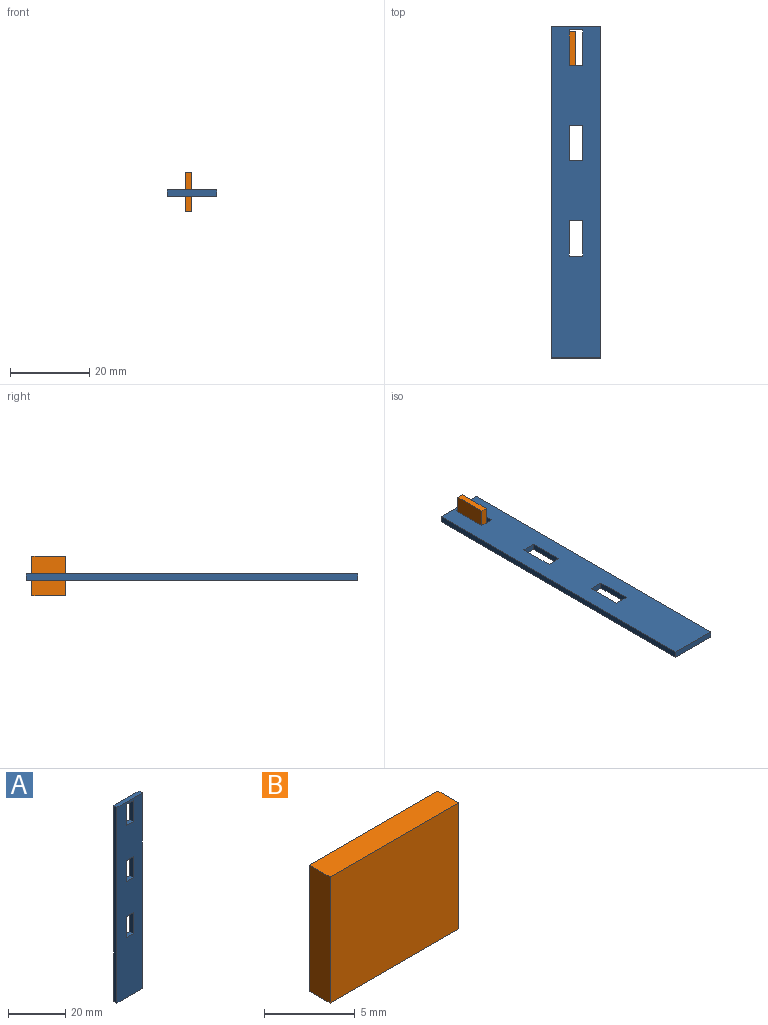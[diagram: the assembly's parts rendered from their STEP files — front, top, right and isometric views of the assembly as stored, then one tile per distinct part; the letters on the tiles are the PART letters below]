
ASSEMBLY  parts=2 mates=2
PART A: 18 faces, bbox 12.5x1.6x83.7 mm
  f0: plane 12.5x1.6mm, normal (0,0,1), area 20mm2, adj f1,f15,f16,f17
  f1: plane 83.71x1.6mm, normal (-1,0,0), area 133.9mm2, adj f0,f2,f16,f17
  f2: plane 12.5x1.6mm, normal (0,0,-1), area 20mm2, adj f1,f15,f16,f17
  f3: plane 9x1.6mm, normal (1,0,0), area 14.4mm2, adj f4,f12,f16,f17
  f4: plane 3.5x1.6mm, normal (0,0,-1), area 5.6mm2, adj f3,f5,f16,f17
  f5: plane 9x1.6mm, normal (-1,0,0), area 14.4mm2, adj f4,f12,f16,f17
  f6: plane 9x1.6mm, normal (1,0,0), area 14.4mm2, adj f7,f13,f16,f17
  f7: plane 3.5x1.6mm, normal (0,0,-1), area 5.6mm2, adj f6,f8,f16,f17
  f8: plane 9x1.6mm, normal (-1,0,0), area 14.4mm2, adj f7,f13,f16,f17
  f9: plane 9x1.6mm, normal (1,0,0), area 14.4mm2, adj f10,f14,f16,f17
  f10: plane 3.5x1.6mm, normal (0,0,-1), area 5.6mm2, adj f9,f11,f16,f17
  f11: plane 9x1.6mm, normal (-1,0,0), area 14.4mm2, adj f10,f14,f16,f17
  f12: plane 3.5x1.6mm, normal (0,0,1), area 5.6mm2, adj f3,f5,f16,f17
  f13: plane 3.5x1.6mm, normal (0,0,1), area 5.6mm2, adj f6,f8,f16,f17
  f14: plane 3.5x1.6mm, normal (0,0,1), area 5.6mm2, adj f9,f11,f16,f17
  f15: plane 83.71x1.6mm, normal (1,0,0), area 133.9mm2, adj f0,f2,f16,f17
  f16: plane 83.71x12.5mm, normal (0,-1,0), area 951.9mm2, adj f0,f1,f2,f3,f4,f5,f6,f7
  f17: plane 83.71x12.5mm, normal (0,1,0), area 951.9mm2, adj f0,f1,f2,f3,f4,f5,f6,f7
PART B: 6 faces, bbox 10x1.6x8.5 mm
  f0: plane 8.5x1.6mm, normal (-1,0,0), area 13.6mm2, adj f1,f3,f4,f5
  f1: plane 10x1.6mm, normal (0,0,-1), area 16mm2, adj f0,f2,f4,f5
  f2: plane 8.5x1.6mm, normal (1,0,0), area 13.6mm2, adj f1,f3,f4,f5
  f3: plane 10x1.6mm, normal (0,0,1), area 16mm2, adj f0,f2,f4,f5
  f4: plane 10x8.5mm, normal (0,-1,0), area 85mm2, adj f0,f1,f2,f3
  f5: plane 10x8.5mm, normal (0,1,0), area 85mm2, adj f0,f1,f2,f3
PLACE A rot(axis=(-1,0,0),90deg) t=(-0.16,-49.32,49.18)mm
PLACE B rot(axis=(-0.58,-0.58,-0.58),120deg) t=(-0.31,-5.58,45.26)mm
MATE planar A.f12 <-> B.f1  axis (0,1,0) through (-0.16,-5.58,49.98)mm
MATE planar B.f4 <-> A.f3  axis (-1,0,0) through (-1.91,-1.33,50.26)mm
